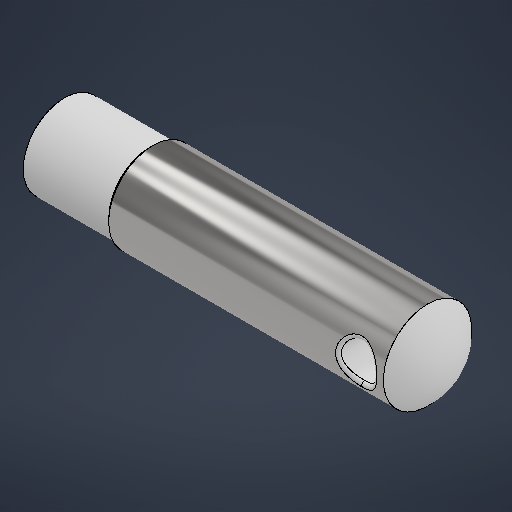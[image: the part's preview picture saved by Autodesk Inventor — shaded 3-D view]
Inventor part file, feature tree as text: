
AUTODESK INVENTOR PART (.ipt)
format: ipt  version: 2025.3 (Build 293356000, 356)  size: 290,304 bytes
history: native  units: mm
features: sketch x1, revolve x1, extrude x1, fillet x1, other x1
ambient origin geometry x8: Origin, YZ Plane, XZ Plane, XY Plane, X Axis, Y Axis, Z Axis, Center Point
bodies: Solid1 (feature_tree)
feature tree (5):
  sketch  "Sketch1"  dims[d0=10.2mm d3=15.0mm d6=50.0mm d8=15.0mm d9=10.0mm d10=6.0mm d11=360.0deg d12=65.0mm d13=0.5mm d14=0.5mm d15=57.0mm d16=0.0mm d17=0.0mm d18=0.5mm d19=14.0mm d20=60.0deg d21=3.385622mm]
  revolve  "Revolution1"  [1 undecoded]
  extrude  "Extrusion1"  Depth=50.0mm
  fillet  "Fillet1"  Radius=15.0mm
  other  "Finish1"
note: 1 required parameter value undecoded (feature->parameter linkage not recoverable at this tier; creation-order binding heuristic only, values carry confidence <= 0.55)
